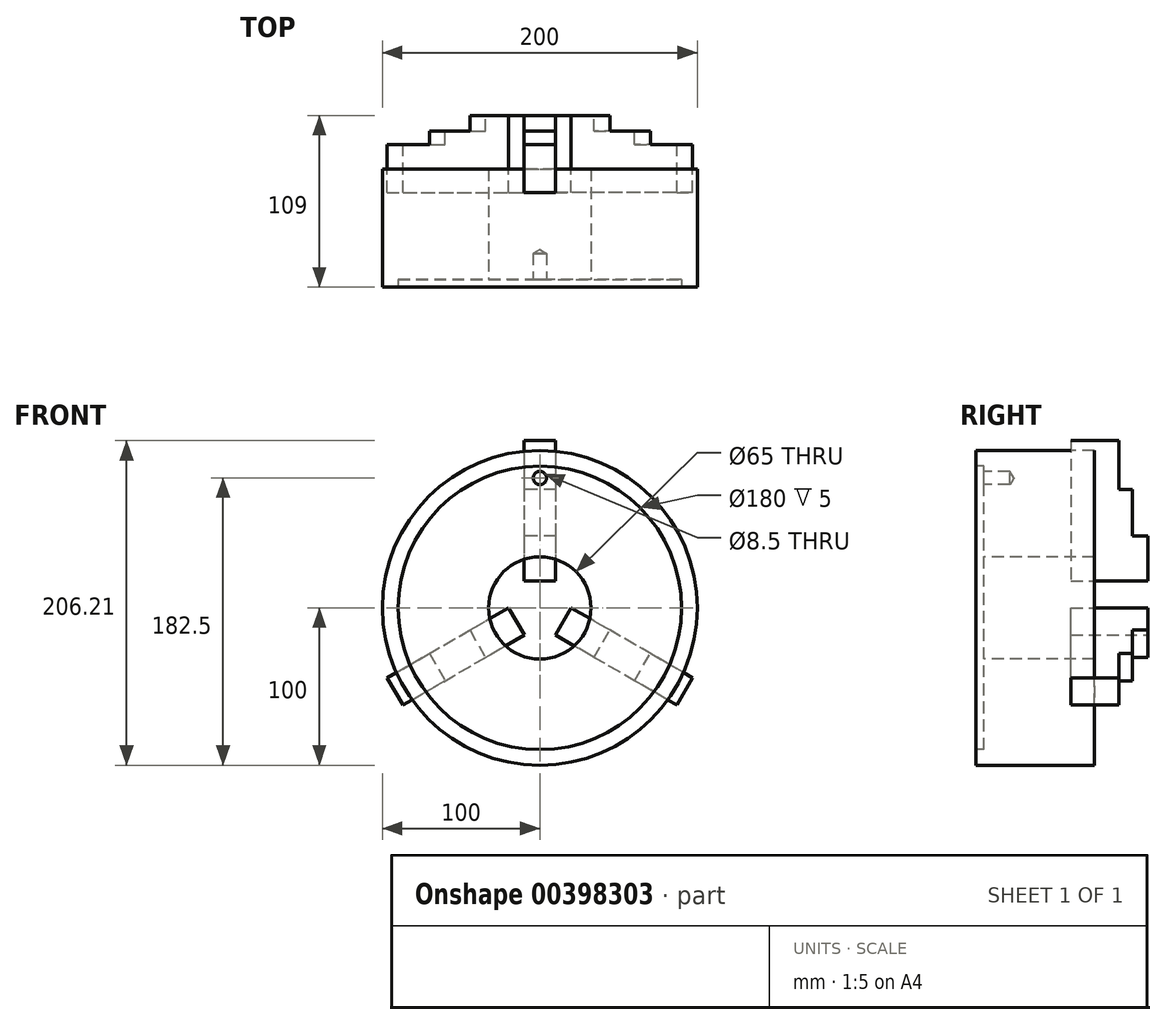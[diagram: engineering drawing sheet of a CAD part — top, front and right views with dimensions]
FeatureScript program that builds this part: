
annotation { "Feature Type Name" : "Feature", "Feature Type Description" : "" }
export const myFeature = defineFeature(function(context is Context, id is Id, definition is map)
    precondition{}
    {
        {
            var Q0;
            Q0=qCreatedBy(makeId("Front.planeOp"),FACE);
            var sketch = newSketch(context, id + "F0", { "sketchPlane" : qUnion([Q0])});
            skCircle(sketch, "E0", {"center": v(0, 0) * mm, "radius": 100 * mm});
            skCircle(sketch, "E1", {"center": v(0, 0) * mm, "radius": 90 * mm});
            skCircle(sketch, "E2", {"center": v(0, 0) * mm, "radius": 82.5 * mm, "construction": true});
            skCircle(sketch, "E3", {"center": v(0, 0) * mm, "radius": 32.5 * mm});
            skPoint(sketch, "E4", {"position": v(0, 82.5) * mm});
            skSolve(sketch);
        }
        {
            var Q0;
            Q0=makeQuery(id+"F0.imprint","IMPRINT",FACE,{"disambiguationData":[TD([[makeQuery(id+"F0.imprint","IMPRINT",EDGE,{"derivedFrom":sQuery(id+"F0.wireOp",EDGE,"E0")}),1.0]])]});
            var Q1;
            Q1=makeQuery(id+"F0.imprint","IMPRINT",FACE,{"disambiguationData":[TD([[makeQuery(id+"F0.imprint","IMPRINT",EDGE,{"derivedFrom":sQuery(id+"F0.wireOp",EDGE,"E1")}),1.0]])]});
            extrude(context, id + "F1", {"entities" : qUnion([Q0, Q1]), "oppositeDirection" : true, "depth" : 75 * mm});
        }
        {
            var Q0;
            Q0=makeQuery(id+"F0.imprint","IMPRINT",FACE,{"disambiguationData":[TD([[makeQuery(id+"F0.imprint","IMPRINT",EDGE,{"derivedFrom":sQuery(id+"F0.wireOp",EDGE,"E1")}),1.0]])]});
            extrude(context, id + "F2", {"entities" : qUnion([Q0]), "operationType" : NewBodyOperationType.REMOVE, "oppositeDirection" : true, "depth" : 5 * mm});
        }
        {
            var Q0;
            Q0=qCreatedBy(makeId("Right.planeOp"),FACE);
            var sketch = newSketch(context, id + "F3", { "sketchPlane" : qUnion([Q0])});
            skLineSegment(sketch, "E5.bottom", {"start": v(60.17, 106.2) * mm, "end": v(90.68, 106.2) * mm});
            skLineSegment(sketch, "E5.left", {"start": v(60.17, 106.2) * mm, "end": v(60.17, 17.1) * mm});
            skLineSegment(sketch, "E5.right", {"start": v(90.68, 106.2) * mm, "end": v(90.68, 75.21) * mm});
            skLineSegment(sketch, "E6.bottom", {"start": v(90.68, 75.21) * mm, "end": v(99.26, 75.21) * mm});
            skLineSegment(sketch, "E6.left", {"start": v(99.26, 75.21) * mm, "end": v(99.26, 45.6) * mm});
            skLineSegment(sketch, "E7.bottom", {"start": v(99.26, 45.6) * mm, "end": v(109, 45.6) * mm});
            skLineSegment(sketch, "E7.top", {"start": v(60.17, 17.1) * mm, "end": v(109, 17.1) * mm});
            skLineSegment(sketch, "E7.right", {"start": v(109, 45.6) * mm, "end": v(109, 17.1) * mm});
            skLineSegment(sketch, "E8.0", {"start": v(0, -100) * mm, "end": v(0, 100) * mm});
            skSolve(sketch);
        }
        {
            var Q0;
            {var subQ1=sQuery(id+"F3.wireOp",EDGE,"E5.bottom");Q0=makeQuery(id+"F3.imprint","IMPRINT",FACE,{"disambiguationData":[TD([[makeQuery(id+"F3.imprint","IMPRINT",EDGE,{"derivedFrom":subQ1}),-1.0]])]});}
            var Q1;
            {var subQ0=sQuery(id+"F3.wireOp",EDGE,"E5.right");var subQ1=sQuery(id+"F3.wireOp",EDGE,"E5.top");var subQ2=makeQuery(id+"F3.imprint","INTERSECT",VERTEX,{"derivedFrom":[subQ1,subQ0]});Q1=makeQuery(id+"F3.imprint","IMPRINT",FACE,{"disambiguationData":[TD([[makeQuery(id+"F3.imprint","IMPRINT",EDGE,{"disambiguationData":[TD([[subQ2,1.0]])],"derivedFrom":subQ1}),1.0]])]});}
            var Q2;
            {var subQ1=sQuery(id+"F3.wireOp",EDGE,"E5.top");var subQ5=sQuery(id+"F3.wireOp",EDGE,"E5.right");var subQ6=makeQuery(id+"F3.imprint","INTERSECT",VERTEX,{"derivedFrom":[subQ1,subQ5]});Q2=makeQuery(id+"F3.imprint","IMPRINT",FACE,{"disambiguationData":[TD([[makeQuery(id+"F3.imprint","IMPRINT",EDGE,{"disambiguationData":[TD([[subQ6,1.0]])],"derivedFrom":subQ1}),-1.0]])]});}
            var Q3;
            {var subQ4=sQuery(id+"F3.wireOp",EDGE,"E6.top");Q3=makeQuery(id+"F3.imprint","IMPRINT",FACE,{"disambiguationData":[TD([[makeQuery(id+"F3.imprint","IMPRINT",EDGE,{"derivedFrom":subQ4}),-1.0]])]});}
            var Q4;
            {var subQ0=sQuery(id+"F3.wireOp",EDGE,"E6.top");Q4=makeQuery(id+"F3.imprint","IMPRINT",FACE,{"disambiguationData":[TD([[makeQuery(id+"F3.imprint","IMPRINT",EDGE,{"derivedFrom":subQ0}),1.0]])]});}
            extrude(context, id + "F4", {"entities" : qUnion([Q0, Q1, Q2, Q3, Q4]), "endBound" : BoundingType.SYMMETRIC, "depth" : 20 * mm});
        }
        {
            var Q0;
            Q0=makeQuery(id+"F4.opExtrude","SWEPT_BODY",BODY,{"disambiguationData":[OSD([sQuery(id+"F3.wireOp",EDGE,"E5.bottom"),sQuery(id+"F3.wireOp",EDGE,"E5.left"),sQuery(id+"F3.wireOp",EDGE,"E5.right"),sQuery(id+"F3.wireOp",EDGE,"E6.bottom"),sQuery(id+"F3.wireOp",EDGE,"E6.left"),sQuery(id+"F3.wireOp",EDGE,"E7.bottom"),sQuery(id+"F3.wireOp",EDGE,"E7.top"),sQuery(id+"F3.wireOp",EDGE,"E7.right")])]});
            var Q1;
            Q1=makeQuery(id+"F1.opExtrude","SWEPT_FACE",FACE,{"disambiguationData":[OSD([sQuery(id+"F0.wireOp",EDGE,"E3")])]});
            circularPattern(context, id + "F5", {"entities" : qUnion([Q0]), "axis" : qUnion([Q1]), "angle" : 360 * degree, "instanceCount" : 3, "equalSpace" : true});
        }
        {
            var Q0;
            Q0=sQuery(id+"F0.wireOp",VERTEX,"E4");
            var Q1;
            Q1=makeQuery(id+"F1.opExtrude","SWEPT_BODY",BODY,{"disambiguationData":[OSD([sQuery(id+"F0.wireOp",EDGE,"E0"),sQuery(id+"F0.wireOp",EDGE,"E3")])]});
            hole(context, id + "F6", {"style" : HoleStyle.SIMPLE, "endStyle" : HoleEndStyle.BLIND, "standardTappedOrClearance" : lookupTablePath({ "standard" : "ISO", "engagement" : "75%", "pitch" : "1.5 mm", "size" : "M10", "type" : "Tapped" }), "standardBlindInLast" : lookupTablePath({ "standard" : "ISO", "engagement" : "75%", "pitch" : "1.5 mm", "size" : "M10", "type" : "Tapped" }), "holeDiameter" : 8.5 * mm, "showTappedDepth" : true, "holeDepth" : 16.5 * mm, "isTappedThrough" : true, "tappedDepth" : 12 * mm, "tapClearance" : 3, "locations" : qUnion([Q0]), "scope" : qUnion([Q1]), "majorDiameter" : 10 * mm});
        }
    });
